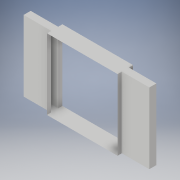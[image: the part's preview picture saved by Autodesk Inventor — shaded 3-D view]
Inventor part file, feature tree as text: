
AUTODESK INVENTOR PART (.ipt)
format: ipt  version: 2017 (Build 210142000, 142)  size: 151,552 bytes
history: native  units: in
note: dims shown in document units (in); Inventor stores cm internally (conversion verified against a paired STEP export)
features: extrude x4, sketch x4, other x1, mirror x1, delete_face x1
ambient origin geometry x8: Origin, YZ Plane, XZ Plane, XY Plane, X Axis, Y Axis, Z Axis, Center Point
bodies: Solid1 (feature_tree)
feature tree (11):
  extrude  "door frame"  Depth=9.0in
  extrude  "door slots"  Depth=1.98in TaperAngle=0.0deg
  extrude  "slot for door"  Depth=0.9in TaperAngle=0.0deg
  extrude  "cap for door slot"  [1 undecoded]
  other  "middle of door"
  mirror  "Mirror2"
  delete_face  "Delete Face3"
  sketch  "Sketch1"  dims[d0=9.0in d1=9.0in]
  sketch  "Sketch2"  dims[d2=1.0in d3=1.98in d4=0.0in]
  sketch  "Sketch5"  dims[d5=0.9in d6=0.0in d11=2.5in d12=0.0in]
  sketch  "Sketch6"  dims[d13=1.0in d14=0.0in]
note: 1 required parameter value undecoded (feature->parameter linkage not recoverable at this tier; creation-order binding heuristic only, values carry confidence <= 0.55)
